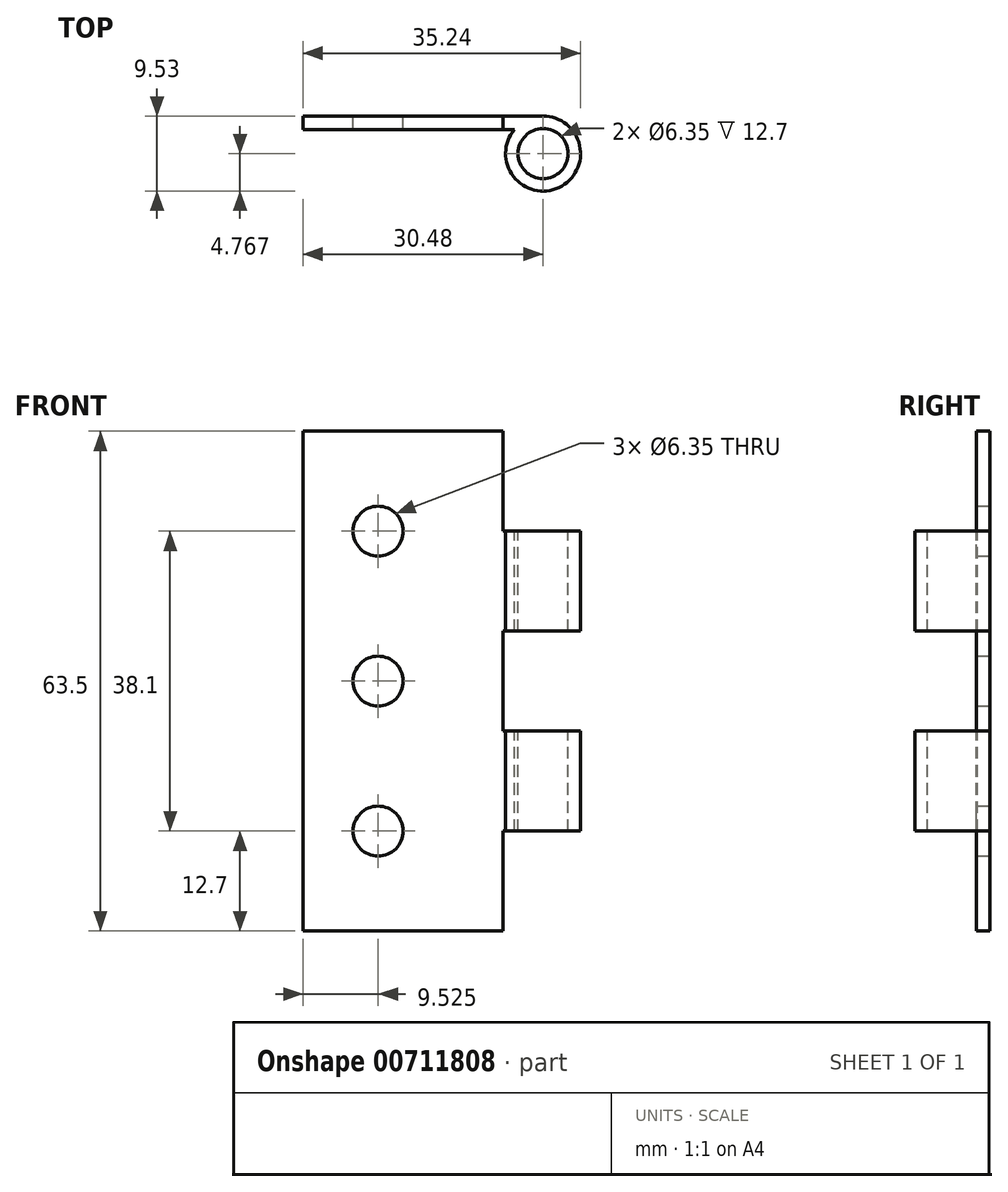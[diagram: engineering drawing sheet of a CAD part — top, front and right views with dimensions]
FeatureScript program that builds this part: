
annotation { "Feature Type Name" : "Feature", "Feature Type Description" : "" }
export const myFeature = defineFeature(function(context is Context, id is Id, definition is map)
    precondition{}
    {
        {
            var Q0;
            Q0=qCreatedBy(makeId("Front.planeOp"),FACE);
            var sketch = newSketch(context, id + "F0", { "sketchPlane" : qUnion([Q0])});
            skLineSegment(sketch, "E0.bottom", {"start": v(0, 0) * mm, "end": v(25.4, 0) * mm});
            skLineSegment(sketch, "E0.top", {"start": v(0, 63.5) * mm, "end": v(25.4, 63.5) * mm});
            skLineSegment(sketch, "E0.left", {"start": v(0, 0) * mm, "end": v(0, 63.5) * mm});
            skLineSegment(sketch, "E0.right", {"start": v(25.4, 0) * mm, "end": v(25.4, 12.7) * mm});
            skLineSegment(sketch, "E1.bottom", {"start": v(25.4, 50.8) * mm, "end": v(33.65, 50.8) * mm});
            skLineSegment(sketch, "E1.top", {"start": v(25.4, 38.1) * mm, "end": v(33.65, 38.1) * mm});
            skLineSegment(sketch, "E1.right", {"start": v(33.65, 50.8) * mm, "end": v(33.65, 38.1) * mm});
            skLineSegment(sketch, "E2.bottom", {"start": v(25.4, 25.4) * mm, "end": v(33.66, 25.4) * mm});
            skLineSegment(sketch, "E2.top", {"start": v(25.4, 12.7) * mm, "end": v(33.66, 12.7) * mm});
            skLineSegment(sketch, "E2.right", {"start": v(33.66, 25.4) * mm, "end": v(33.66, 12.7) * mm});
            skLineSegment(sketch, "E3.trimOffspring", {"start": v(25.4, 25.4) * mm, "end": v(25.4, 38.1) * mm});
            skLineSegment(sketch, "E4.trimOffspring", {"start": v(25.4, 50.8) * mm, "end": v(25.4, 63.5) * mm});
            skCircle(sketch, "E5", {"center": v(9.52, 50.8) * mm, "radius": 3.18 * mm});
            skCircle(sketch, "E6", {"center": v(9.52, 31.75) * mm, "radius": 3.18 * mm});
            skCircle(sketch, "E7", {"center": v(9.53, 12.7) * mm, "radius": 3.18 * mm});
            skSolve(sketch);
        }
        {
            var Q0;
            Q0 = qSketchRegion(id + "F0", true);
            extrude(context, id + "F1", {"entities" : qUnion([Q0]), "depth" : 1.71 * mm, "offsetDistance" : 25.4 * mm});
        }
        {
            var Q0;
            Q0=makeQuery(id+"F1.opExtrude","SWEPT_FACE",FACE,{"disambiguationData":[OSD([sQuery(id+"F0.wireOp",EDGE,"E1.bottom")])]});
            var sketch = newSketch(context, id + "F2", { "sketchPlane" : qUnion([Q0])});
            skCircle(sketch, "E8", {"center": v(30.48, -4.76) * mm, "radius": 4.76 * mm});
            skSolve(sketch);
        }
        {
            var Q0;
            Q0 = qSketchRegion(id + "F2", true);
            extrude(context, id + "F3", {"entities" : qUnion([Q0]), "operationType" : NewBodyOperationType.ADD, "oppositeDirection" : true, "depth" : 38.1 * mm, "offsetDistance" : 25.4 * mm});
        }
        {
            var Q0;
            Q0=makeQuery(id+"F3.boolean.opBoolean","MERGE",FACE,{"derivedFrom":[makeQuery(id+"F1.opExtrude","SWEPT_FACE",FACE,{"disambiguationData":[OSD([sQuery(id+"F0.wireOp",EDGE,"E1.bottom")])]}),makeQuery(id+"F3.opExtrude","CAP_FACE",FACE,{"disambiguationData":[OSD([sQuery(id+"F2.wireOp",EDGE,"E8")])],"isStart":true})]});
            var sketch = newSketch(context, id + "F4", { "sketchPlane" : qUnion([Q0])});
            skCircle(sketch, "E9", {"center": v(30.48, -4.76) * mm, "radius": 4.76 * mm});
            skLineSegment(sketch, "E10", {"start": v(33.65, 0) * mm, "end": v(33.65, -1.21) * mm});
            skLineSegment(sketch, "E11", {"start": v(33.65, 0) * mm, "end": v(30.48, 0) * mm});
            skCircle(sketch, "E12", {"center": v(30.48, -4.76) * mm, "radius": 3.18 * mm});
            skSolve(sketch);
        }
        {
            var Q0;
            Q0=makeQuery(id+"F4.imprint","IMPRINT",FACE,{"disambiguationData":[TD([[makeQuery(id+"F4.imprint","IMPRINT",EDGE,{"derivedFrom":sQuery(id+"F4.wireOp",EDGE,"E12")}),1.0]])]});
            var Q1;
            {var subQ0=sQuery(id+"F4.wireOp",EDGE,"E10");Q1=makeQuery(id+"F4.imprint","IMPRINT",FACE,{"disambiguationData":[TD([[makeQuery(id+"F4.imprint","IMPRINT",EDGE,{"derivedFrom":subQ0}),1.0]])]});}
            extrude(context, id + "F5", {"entities" : qUnion([Q0, Q1]), "operationType" : NewBodyOperationType.REMOVE, "oppositeDirection" : true, "depth" : 38.1 * mm, "offsetDistance" : 25.4 * mm});
        }
        {
            var Q0;
            Q0=makeQuery(id+"F1.opExtrude","CAP_FACE",FACE,{"disambiguationData":[OSD([sQuery(id+"F0.wireOp",EDGE,"E0.bottom"),sQuery(id+"F0.wireOp",EDGE,"E0.top"),sQuery(id+"F0.wireOp",EDGE,"E0.left"),sQuery(id+"F0.wireOp",EDGE,"E0.right"),sQuery(id+"F0.wireOp",EDGE,"E1.bottom"),sQuery(id+"F0.wireOp",EDGE,"E1.top"),sQuery(id+"F0.wireOp",EDGE,"E1.right"),sQuery(id+"F0.wireOp",EDGE,"E2.bottom"),sQuery(id+"F0.wireOp",EDGE,"E2.top"),sQuery(id+"F0.wireOp",EDGE,"E2.right"),sQuery(id+"F0.wireOp",EDGE,"E3.trimOffspring"),sQuery(id+"F0.wireOp",EDGE,"E4.trimOffspring"),sQuery(id+"F0.wireOp",EDGE,"E5"),sQuery(id+"F0.wireOp",EDGE,"E6"),sQuery(id+"F0.wireOp",EDGE,"E7")])],"isStart":true});
            var sketch = newSketch(context, id + "F6", { "sketchPlane" : qUnion([Q0])});
            skLineSegment(sketch, "E13.bottom", {"start": v(-25.4, 38.1) * mm, "end": v(-38.47, 38.1) * mm});
            skLineSegment(sketch, "E13.top", {"start": v(-25.4, 25.4) * mm, "end": v(-38.47, 25.4) * mm});
            skLineSegment(sketch, "E13.left", {"start": v(-25.4, 38.1) * mm, "end": v(-25.4, 25.4) * mm});
            skLineSegment(sketch, "E13.right", {"start": v(-38.47, 38.1) * mm, "end": v(-38.47, 25.4) * mm});
            skSolve(sketch);
        }
        {
            var Q0;
            Q0 = qSketchRegion(id + "F6", true);
            extrude(context, id + "F7", {"entities" : qUnion([Q0]), "operationType" : NewBodyOperationType.REMOVE, "oppositeDirection" : true, "depth" : 25.4 * mm, "offsetDistance" : 25.4 * mm});
        }
    });
